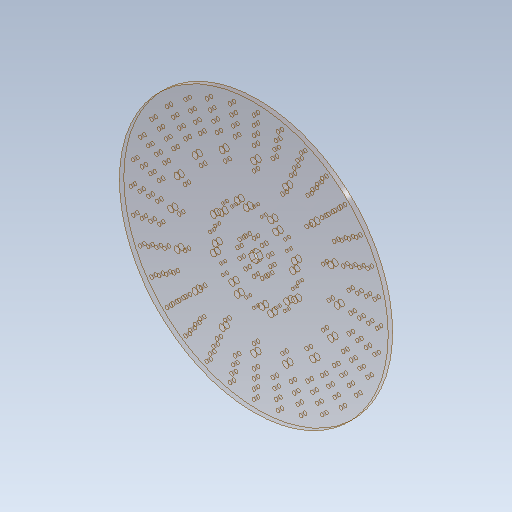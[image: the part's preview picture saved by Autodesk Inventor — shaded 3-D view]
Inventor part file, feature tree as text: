
AUTODESK INVENTOR PART (.ipt)
format: ipt  version: 2020 (Build 240168000, 168)  size: 452,608 bytes
history: native  units: in
note: dims shown in document units (in); Inventor stores cm internally (conversion verified against a paired STEP export)
features: other x3, sketch x3
ambient origin geometry x8: Origin, YZ Plane, XZ Plane, XY Plane, X Axis, Y Axis, Z Axis, Center Point
bodies: Solid1 (feature_tree)
feature tree (6):
  other  "IndexWheelFlatPlatesPolyInside.ipt"
  other  "Solid1::IndexWheelFlatPlatesPolyInside.ipt"
  other  "TaggingFeature1"
  sketch  "Sketch1"  dims[d0=0.3937in]
  sketch  "Sketch2"
  sketch  "Sketch3"
